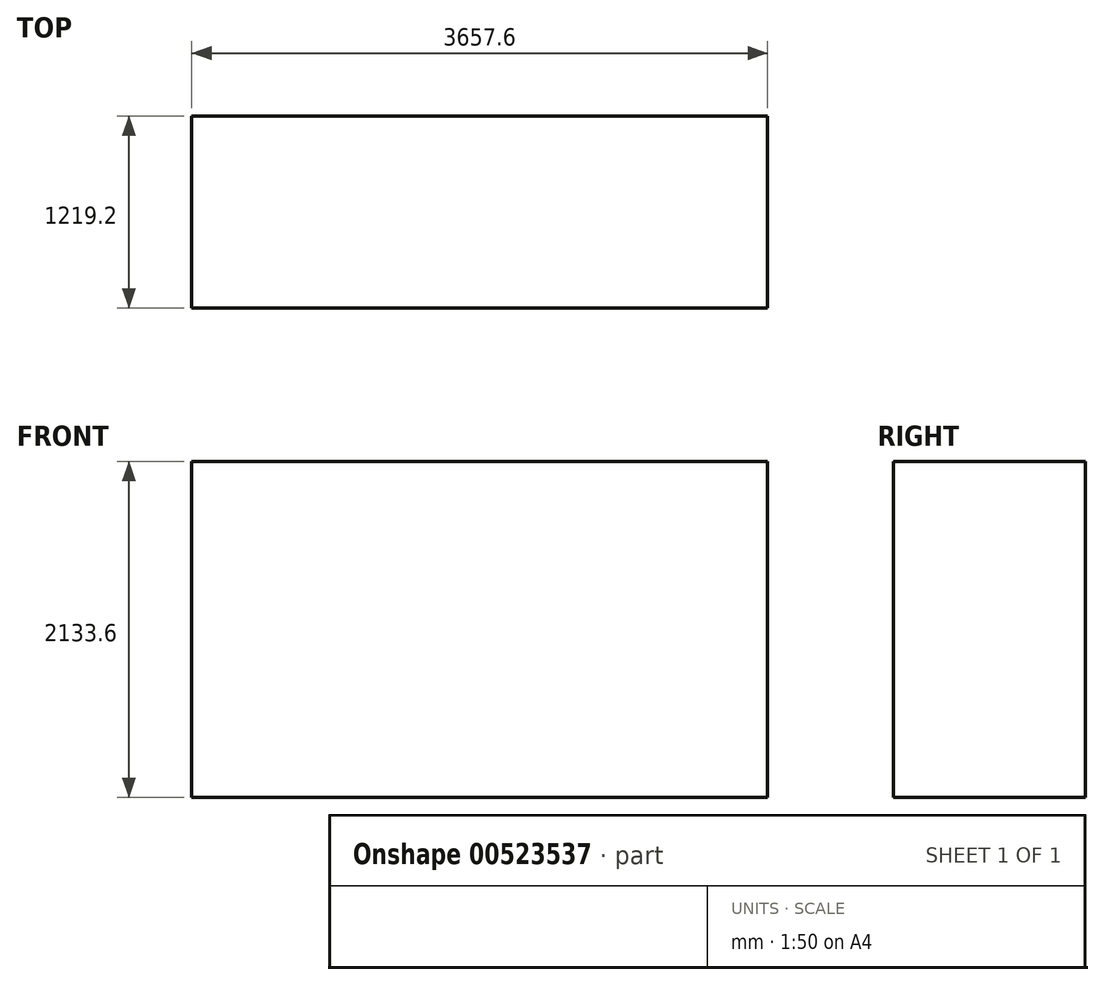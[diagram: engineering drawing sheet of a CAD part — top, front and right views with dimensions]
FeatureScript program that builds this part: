
annotation { "Feature Type Name" : "Feature", "Feature Type Description" : "" }
export const myFeature = defineFeature(function(context is Context, id is Id, definition is map)
    precondition{}
    {
        {
            var Q0;
            Q0=qCreatedBy(makeId("Front.planeOp"),FACE);
            var sketch = newSketch(context, id + "F0", { "sketchPlane" : qUnion([Q0])});
            skLineSegment(sketch, "E0.bottom", {"start": v(3657.6, 0) * mm, "end": v(0, 0) * mm});
            skLineSegment(sketch, "E0.top", {"start": v(3657.6, 2133.6) * mm, "end": v(0, 2133.6) * mm});
            skLineSegment(sketch, "E0.left", {"start": v(3657.6, 0) * mm, "end": v(3657.6, 2133.6) * mm});
            skLineSegment(sketch, "E0.right", {"start": v(0, 0) * mm, "end": v(0, 2133.6) * mm});
            skSolve(sketch);
        }
        {
            var Q0;
            Q0 = qSketchRegion(id + "F0", true);
            extrude(context, id + "F1", {"entities" : qUnion([Q0]), "depth" : 1219.2 * mm, "offsetDistance" : 25.4 * mm});
        }
    });
